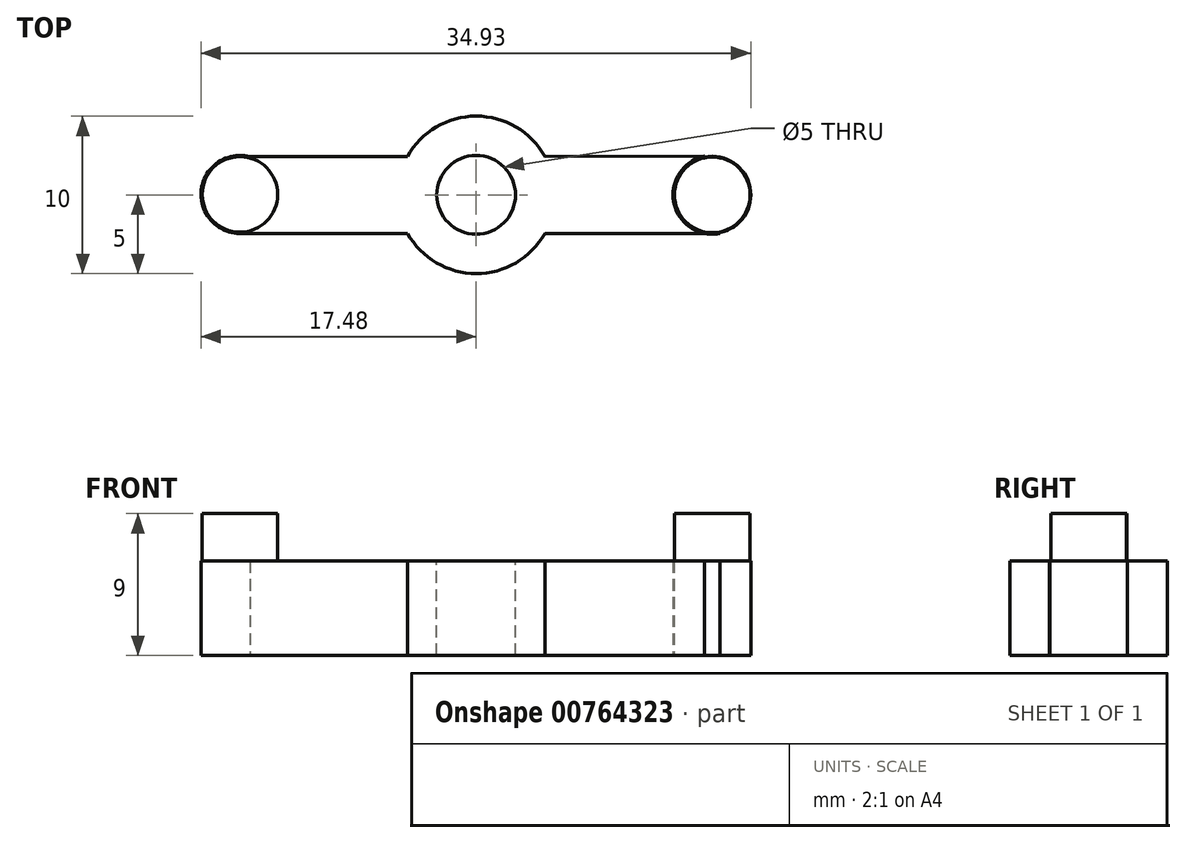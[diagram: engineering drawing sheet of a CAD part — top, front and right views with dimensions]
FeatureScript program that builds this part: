
annotation { "Feature Type Name" : "Feature", "Feature Type Description" : "" }
export const myFeature = defineFeature(function(context is Context, id is Id, definition is map)
    precondition{}
    {
        {
            var Q0;
            Q0=qCreatedBy(makeId("Top.planeOp"),FACE);
            var sketch = newSketch(context, id + "F0", { "sketchPlane" : qUnion([Q0])});
            skCircle(sketch, "E0", {"center": v(0, 0) * mm, "radius": 2.5 * mm, "construction": true});
            skCircle(sketch, "E1.0.1.0", {"center": v(0, 15) * mm, "radius": 2.5 * mm, "construction": true});
            skCircle(sketch, "E1.0.2.0", {"center": v(0, 30) * mm, "radius": 2.5 * mm, "construction": true});
            skCircle(sketch, "E1.1.0.0", {"center": v(15, 0) * mm, "radius": 2.5 * mm, "construction": true});
            skCircle(sketch, "E1.1.1.0", {"center": v(15, 15) * mm, "radius": 2.5 * mm, "construction": true});
            skCircle(sketch, "E1.1.2.0", {"center": v(15, 30) * mm, "radius": 2.5 * mm, "construction": true});
            skCircle(sketch, "E1.2.0.0", {"center": v(30, 0) * mm, "radius": 2.5 * mm, "construction": true});
            skCircle(sketch, "E1.2.1.0", {"center": v(30, 15) * mm, "radius": 2.5 * mm, "construction": true});
            skCircle(sketch, "E1.2.2.0", {"center": v(30, 30) * mm, "radius": 2.5 * mm, "construction": true});
            skLineSegment(sketch, "E1.direction1", {"start": v(0, 0) * mm, "end": v(15, 0) * mm, "construction": true});
            skLineSegment(sketch, "E1.direction2", {"start": v(0, 0) * mm, "end": v(0, 15) * mm, "construction": true});
            skCircle(sketch, "E2", {"center": v(0, 15) * mm, "radius": 2.45 * mm});
            skCircle(sketch, "E3", {"center": v(30, 15) * mm, "radius": 2.45 * mm});
            skLineSegment(sketch, "E4", {"start": v(0.63, 17.42) * mm, "end": v(10.63, 17.43) * mm});
            skLineSegment(sketch, "E5", {"start": v(0, 12.55) * mm, "end": v(30.5, 12.55) * mm});
            skCircle(sketch, "E6", {"center": v(15, 15) * mm, "radius": 5 * mm});
            skLineSegment(sketch, "E7.trimOffspring", {"start": v(14.43, 17.43) * mm, "end": v(15.57, 17.43) * mm});
            skLineSegment(sketch, "E8.trimOffspring", {"start": v(19.37, 17.44) * mm, "end": v(29.5, 17.45) * mm});
            skArc(sketch, "E9", {"start": v(0.63, 17.42) * mm, "mid": v(-2.45, 15.34) * mm, "end": v(0, 12.55) * mm});
            skArc(sketch, "E10", {"start": v(29.5, 17.45) * mm, "mid": v(28.42, 13.06) * mm, "end": v(32.5, 15) * mm});
            skSolve(sketch);
        }
        {
            var Q0;
            Q0=makeQuery(id+"F0.imprint","IMPRINT",FACE,{"disambiguationData":[TD([[makeQuery(id+"F0.imprint","IMPRINT",EDGE,{"derivedFrom":sQuery(id+"F0.wireOp",EDGE,"E3")}),1.0]])]});
            var Q1;
            {var subQ0=sQuery(id+"F0.wireOp",EDGE,"E10");var subQ1=sQuery(id+"F0.wireOp",EDGE,"E5");var subQ2=makeQuery(id+"F0.imprint","INTERSECT",VERTEX,{"disambiguationData":[OD(0.0)],"derivedFrom":[subQ1,subQ0]});Q1=makeQuery(id+"F0.imprint","IMPRINT",FACE,{"disambiguationData":[TD([[makeQuery(id+"F0.imprint","IMPRINT",EDGE,{"disambiguationData":[TD([[subQ2,1.0]])],"derivedFrom":subQ1}),-1.0]])]});}
            var Q2;
            {var subQ0=sQuery(id+"F0.wireOp",EDGE,"E2");var subQ1=makeQuery(id+"F0.imprint","INTERSECT",VERTEX,{"derivedFrom":[subQ0,sQuery(id+"F0.wireOp",EDGE,"E5")]});Q2=makeQuery(id+"F0.imprint","IMPRINT",FACE,{"disambiguationData":[TD([[makeQuery(id+"F0.imprint","IMPRINT",EDGE,{"disambiguationData":[TD([[subQ1,1.0]])],"derivedFrom":subQ0}),1.0]])]});}
            var Q3;
            {var subQ0=sQuery(id+"F0.wireOp",EDGE,"E6");var subQ1=sQuery(id+"F0.wireOp",EDGE,"E5");var subQ2=makeQuery(id+"F0.imprint","INTERSECT",VERTEX,{"disambiguationData":[OD(0.0)],"derivedFrom":[subQ1,subQ0]});Q3=makeQuery(id+"F0.imprint","IMPRINT",FACE,{"disambiguationData":[TD([[makeQuery(id+"F0.imprint","IMPRINT",EDGE,{"disambiguationData":[TD([[subQ2,-1.0]])],"derivedFrom":subQ1}),-1.0]])]});}
            var Q4;
            {var subQ5=sQuery(id+"F0.wireOp",EDGE,"E8.trimOffspring");Q4=makeQuery(id+"F0.imprint","IMPRINT",FACE,{"disambiguationData":[TD([[makeQuery(id+"F0.imprint","IMPRINT",EDGE,{"derivedFrom":subQ5}),-1.0]])]});}
            var Q5;
            {var subQ0=sQuery(id+"F0.wireOp",EDGE,"E6");var subQ1=sQuery(id+"F0.wireOp",EDGE,"E5");var subQ2=makeQuery(id+"F0.imprint","INTERSECT",VERTEX,{"disambiguationData":[OD(0.0)],"derivedFrom":[subQ1,subQ0]});Q5=makeQuery(id+"F0.imprint","IMPRINT",FACE,{"disambiguationData":[TD([[makeQuery(id+"F0.imprint","IMPRINT",EDGE,{"disambiguationData":[TD([[subQ2,-1.0]])],"derivedFrom":subQ1}),1.0]])]});}
            var Q6;
            {var subQ1=sQuery(id+"F0.wireOp",EDGE,"E4");Q6=makeQuery(id+"F0.imprint","IMPRINT",FACE,{"disambiguationData":[TD([[makeQuery(id+"F0.imprint","IMPRINT",EDGE,{"derivedFrom":subQ1}),-1.0]])]});}
            extrude(context, id + "F1", {"entities" : qUnion([Q0, Q1, Q2, Q3, Q4, Q5, Q6]), "depth" : 6 * mm, "offsetDistance" : 25 * mm});
        }
        {
            var Q0;
            Q0=makeQuery(id+"F1.opExtrude","CAP_FACE",FACE,{"disambiguationData":[OSD([sQuery(id+"F0.wireOp",EDGE,"E2"),sQuery(id+"F0.wireOp",EDGE,"E4"),sQuery(id+"F0.wireOp",EDGE,"E5"),sQuery(id+"F0.wireOp",EDGE,"E6"),sQuery(id+"F0.wireOp",EDGE,"E8.trimOffspring"),sQuery(id+"F0.wireOp",EDGE,"E9"),sQuery(id+"F0.wireOp",EDGE,"E10")])],"isStart":false});
            var sketch = newSketch(context, id + "F2", { "sketchPlane" : qUnion([Q0])});
            skCircle(sketch, "E11", {"center": v(15, 15) * mm, "radius": 2.5 * mm});
            skCircle(sketch, "E12", {"center": v(0, 15.03) * mm, "radius": 2.4 * mm});
            skCircle(sketch, "E13", {"center": v(30, 15) * mm, "radius": 2.4 * mm});
            skSolve(sketch);
        }
        {
            var Q0;
            Q0=makeQuery(id+"F2.imprint","IMPRINT",FACE,{"disambiguationData":[TD([[makeQuery(id+"F2.imprint","IMPRINT",EDGE,{"derivedFrom":sQuery(id+"F2.wireOp",EDGE,"E11")}),1.0]])]});
            extrude(context, id + "F3", {"entities" : qUnion([Q0]), "operationType" : NewBodyOperationType.REMOVE, "endBound" : BoundingType.THROUGH_ALL, "oppositeDirection" : true, "depth" : 7 * mm, "offsetDistance" : 25 * mm});
        }
        {
            var Q0;
            Q0=makeQuery(id+"F2.imprint","IMPRINT",FACE,{"disambiguationData":[TD([[makeQuery(id+"F2.imprint","IMPRINT",EDGE,{"derivedFrom":sQuery(id+"F2.wireOp",EDGE,"E12")}),1.0]])]});
            var Q1;
            Q1=makeQuery(id+"F2.imprint","IMPRINT",FACE,{"disambiguationData":[TD([[makeQuery(id+"F2.imprint","IMPRINT",EDGE,{"derivedFrom":sQuery(id+"F2.wireOp",EDGE,"E13")}),1.0]])]});
            extrude(context, id + "F4", {"entities" : qUnion([Q0, Q1]), "depth" : 3 * mm, "offsetDistance" : 25 * mm});
        }
    });
